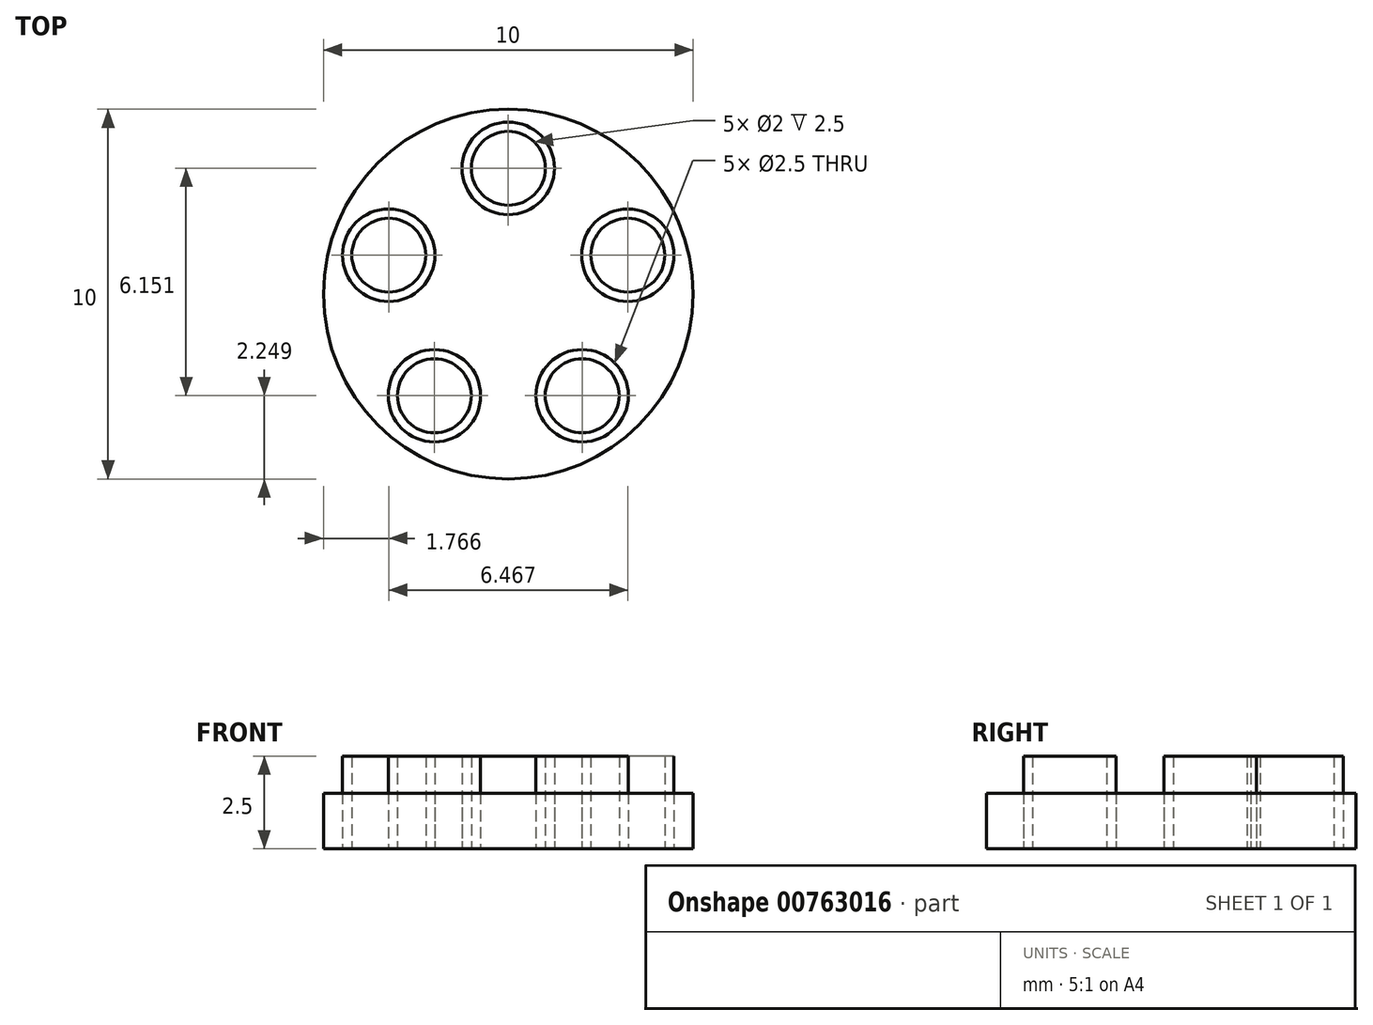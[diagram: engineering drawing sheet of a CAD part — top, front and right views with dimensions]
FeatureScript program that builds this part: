
annotation { "Feature Type Name" : "Feature", "Feature Type Description" : "" }
export const myFeature = defineFeature(function(context is Context, id is Id, definition is map)
    precondition{}
    {
        {
            var Q0;
            Q0=qCreatedBy(makeId("Top.planeOp"),FACE);
            var sketch = newSketch(context, id + "F0", { "sketchPlane" : qUnion([Q0])});
            skCircle(sketch, "E0", {"center": v(0, 0) * mm, "radius": 5 * mm});
            skCircle(sketch, "E1", {"center": v(0, 3.4) * mm, "radius": 1.25 * mm});
            skCircle(sketch, "E2", {"center": v(0, 3.4) * mm, "radius": 1 * mm});
            skCircle(sketch, "E3.1.0", {"center": v(-3.23, 1.05) * mm, "radius": 1 * mm});
            skCircle(sketch, "E3.2.0", {"center": v(-2, -2.75) * mm, "radius": 1 * mm});
            skCircle(sketch, "E3.3.0", {"center": v(2, -2.75) * mm, "radius": 1 * mm});
            skCircle(sketch, "E3.4.0", {"center": v(3.23, 1.05) * mm, "radius": 1 * mm});
            skCircle(sketch, "E4.1.0", {"center": v(-3.23, 1.05) * mm, "radius": 1.25 * mm});
            skCircle(sketch, "E4.2.0", {"center": v(-2, -2.75) * mm, "radius": 1.25 * mm});
            skCircle(sketch, "E4.3.0", {"center": v(2, -2.75) * mm, "radius": 1.25 * mm});
            skCircle(sketch, "E4.4.0", {"center": v(3.23, 1.05) * mm, "radius": 1.25 * mm});
            skSolve(sketch);
        }
        {
            var Q0;
            Q0=makeQuery(id+"F0.imprint","IMPRINT",FACE,{"disambiguationData":[TD([[makeQuery(id+"F0.imprint","IMPRINT",EDGE,{"derivedFrom":sQuery(id+"F0.wireOp",EDGE,"E3.2.0")}),-1.0]])]});
            var Q1;
            Q1=makeQuery(id+"F0.imprint","IMPRINT",FACE,{"disambiguationData":[TD([[makeQuery(id+"F0.imprint","IMPRINT",EDGE,{"derivedFrom":sQuery(id+"F0.wireOp",EDGE,"E3.1.0")}),-1.0]])]});
            var Q2;
            Q2=makeQuery(id+"F0.imprint","IMPRINT",FACE,{"disambiguationData":[TD([[makeQuery(id+"F0.imprint","IMPRINT",EDGE,{"derivedFrom":sQuery(id+"F0.wireOp",EDGE,"E3.3.0")}),-1.0]])]});
            var Q3;
            Q3=makeQuery(id+"F0.imprint","IMPRINT",FACE,{"disambiguationData":[TD([[makeQuery(id+"F0.imprint","IMPRINT",EDGE,{"derivedFrom":sQuery(id+"F0.wireOp",EDGE,"E3.4.0")}),-1.0]])]});
            var Q4;
            Q4=makeQuery(id+"F0.imprint","IMPRINT",FACE,{"disambiguationData":[TD([[makeQuery(id+"F0.imprint","IMPRINT",EDGE,{"derivedFrom":sQuery(id+"F0.wireOp",EDGE,"E1")}),1.0]])]});
            extrude(context, id + "F1", {"entities" : qUnion([Q0, Q1, Q2, Q3, Q4]), "depth" : 2.5 * mm, "offsetDistance" : 25 * mm});
        }
        {
            var Q0;
            Q0=makeQuery(id+"F0.imprint","IMPRINT",FACE,{"disambiguationData":[TD([[makeQuery(id+"F0.imprint","IMPRINT",EDGE,{"derivedFrom":sQuery(id+"F0.wireOp",EDGE,"E0")}),1.0]])]});
            extrude(context, id + "F2", {"entities" : qUnion([Q0]), "depth" : 1.5 * mm, "offsetDistance" : 25 * mm});
        }
    });
